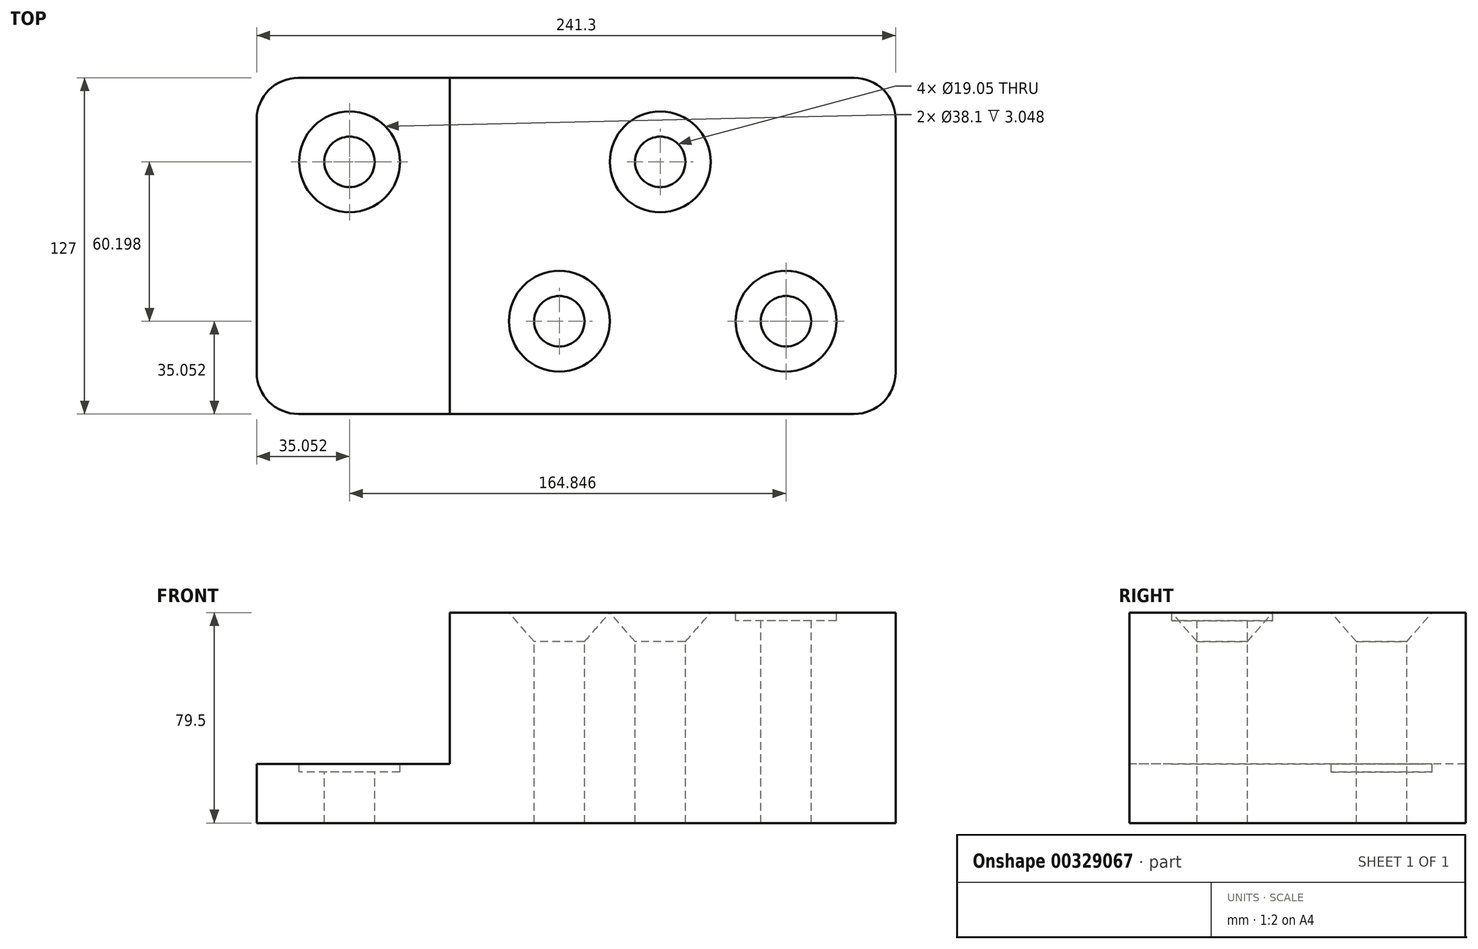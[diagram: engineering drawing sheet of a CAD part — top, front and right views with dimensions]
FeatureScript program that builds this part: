
annotation { "Feature Type Name" : "Feature", "Feature Type Description" : "" }
export const myFeature = defineFeature(function(context is Context, id is Id, definition is map)
    precondition{}
    {
        {
            var Q0;
            Q0=qCreatedBy(makeId("Top.planeOp"),FACE);
            var sketch = newSketch(context, id + "F0", { "sketchPlane" : qUnion([Q0])});
            skLineSegment(sketch, "E0.bottom", {"start": v(0, 0) * mm, "end": v(241.3, 0) * mm});
            skLineSegment(sketch, "E0.top", {"start": v(0, 127) * mm, "end": v(241.3, 127) * mm});
            skLineSegment(sketch, "E0.left", {"start": v(0, 0) * mm, "end": v(0, 127) * mm});
            skLineSegment(sketch, "E0.right", {"start": v(241.3, 0) * mm, "end": v(241.3, 127) * mm});
            skSolve(sketch);
        }
        {
            var Q0;
            Q0 = qSketchRegion(id + "F0", true);
            extrude(context, id + "F1", {"entities" : qUnion([Q0]), "depth" : 79.5 * mm});
        }
        {
            var Q0;
            Q0=makeQuery(id+"F1.opExtrude","CAP_FACE",FACE,{"disambiguationData":[OSD([sQuery(id+"F0.wireOp",EDGE,"E0.bottom"),sQuery(id+"F0.wireOp",EDGE,"E0.top"),sQuery(id+"F0.wireOp",EDGE,"E0.left"),sQuery(id+"F0.wireOp",EDGE,"E0.right")])],"isStart":false});
            var sketch = newSketch(context, id + "F2", { "sketchPlane" : qUnion([Q0])});
            skLineSegment(sketch, "E1.bottom", {"start": v(241.3, 127) * mm, "end": v(72.9, 127) * mm});
            skLineSegment(sketch, "E1.top", {"start": v(241.3, 0) * mm, "end": v(72.9, 0) * mm});
            skLineSegment(sketch, "E1.left", {"start": v(241.3, 127) * mm, "end": v(241.3, 0) * mm});
            skLineSegment(sketch, "E1.right", {"start": v(72.9, 127) * mm, "end": v(72.9, 0) * mm});
            skSolve(sketch);
        }
        {
            var Q0;
            {var subQ0=sQuery(id+"F2.wireOp",EDGE,"E1.right");Q0=makeQuery(id+"F2.imprint","IMPRINT",FACE,{"disambiguationData":[TD([[makeQuery(id+"F2.imprint","IMPRINT",EDGE,{"derivedFrom":subQ0}),-1.0]])]});}
            extrude(context, id + "F3", {"entities" : qUnion([Q0]), "operationType" : NewBodyOperationType.REMOVE, "oppositeDirection" : true, "depth" : 57.15 * mm});
        }
        {
            var Q0;
            Q0=makeQuery(id+"F3.boolean.opBoolean","COPY",EDGE,{"derivedFrom":makeQuery(id+"F3.opExtrude","SWEPT_EDGE",EDGE,{"disambiguationData":[OSD([sQuery(id+"F0.wireOp",EDGE,"E0.bottom"),sQuery(id+"F2.wireOp",EDGE,"E1.top"),sQuery(id+"F2.wireOp",EDGE,"E1.right")])]})});
            var Q1;
            Q1=makeQuery(id+"F1.opExtrude","SWEPT_EDGE",EDGE,{"disambiguationData":[OSD([sQuery(id+"F0.wireOp",EDGE,"E0.bottom"),sQuery(id+"F0.wireOp",EDGE,"E0.left")])]});
            var Q2;
            Q2=makeQuery(id+"F1.opExtrude","SWEPT_EDGE",EDGE,{"disambiguationData":[OSD([sQuery(id+"F0.wireOp",EDGE,"E0.top"),sQuery(id+"F0.wireOp",EDGE,"E0.left")])]});
            var Q3;
            Q3=makeQuery(id+"F3.boolean.opBoolean","COPY",EDGE,{"derivedFrom":makeQuery(id+"F3.opExtrude","SWEPT_EDGE",EDGE,{"disambiguationData":[OSD([sQuery(id+"F0.wireOp",EDGE,"E0.top"),sQuery(id+"F2.wireOp",EDGE,"E1.bottom"),sQuery(id+"F2.wireOp",EDGE,"E1.right")])]})});
            var Q4;
            Q4=makeQuery(id+"F1.opExtrude","SWEPT_EDGE",EDGE,{"disambiguationData":[OSD([sQuery(id+"F0.wireOp",EDGE,"E0.bottom"),sQuery(id+"F0.wireOp",EDGE,"E0.right")])]});
            var Q5;
            Q5=makeQuery(id+"F1.opExtrude","SWEPT_EDGE",EDGE,{"disambiguationData":[OSD([sQuery(id+"F0.wireOp",EDGE,"E0.top"),sQuery(id+"F0.wireOp",EDGE,"E0.right")])]});
            fillet(context, id + "F4", {"entities" : qUnion([Q0, Q1, Q2, Q3, Q4, Q5]), "radius" : 15.75 * mm, "tangentPropagation" : true, "allowEdgeOverflow" : false});
        }
        {
            var Q0;
            Q0=makeQuery(id+"F1.opExtrude","CAP_FACE",FACE,{"disambiguationData":[OSD([sQuery(id+"F0.wireOp",EDGE,"E0.bottom"),sQuery(id+"F0.wireOp",EDGE,"E0.top"),sQuery(id+"F0.wireOp",EDGE,"E0.left"),sQuery(id+"F0.wireOp",EDGE,"E0.right")])],"isStart":false});
            var sketch = newSketch(context, id + "F5", { "sketchPlane" : qUnion([Q0])});
            skPoint(sketch, "E2", {"position": v(199.9, 35.05) * mm});
            skPoint(sketch, "E3", {"position": v(152.4, 95.25) * mm});
            skPoint(sketch, "E4", {"position": v(114.3, 35.05) * mm});
            skSolve(sketch);
        }
        {
            var Q0;
            Q0=sQuery(id+"F5.wireOp",VERTEX,"E2");
            var Q1;
            Q1=makeQuery(id+"F1.opExtrude","SWEPT_BODY",BODY,{"disambiguationData":[OSD([sQuery(id+"F0.wireOp",EDGE,"E0.bottom"),sQuery(id+"F0.wireOp",EDGE,"E0.top"),sQuery(id+"F0.wireOp",EDGE,"E0.left"),sQuery(id+"F0.wireOp",EDGE,"E0.right")])]});
            hole(context, id + "F6", {"style" : HoleStyle.C_BORE, "endStyle" : HoleEndStyle.THROUGH, "holeDiameter" : 19.05 * mm, "cBoreDiameter" : 38.1 * mm, "cBoreDepth" : 3.05 * mm, "tappedDepth" : 12.7 * mm, "tapClearance" : 3, "locations" : qUnion([Q0]), "scope" : qUnion([Q1])});
        }
        {
            var Q0;
            Q0=makeQuery(id+"F1.opExtrude","CAP_FACE",FACE,{"disambiguationData":[OSD([sQuery(id+"F0.wireOp",EDGE,"E0.bottom"),sQuery(id+"F0.wireOp",EDGE,"E0.top"),sQuery(id+"F0.wireOp",EDGE,"E0.left"),sQuery(id+"F0.wireOp",EDGE,"E0.right")])],"isStart":false});
            var sketch = newSketch(context, id + "F7", { "sketchPlane" : qUnion([Q0])});
            skPoint(sketch, "E5", {"position": v(152.4, 95.25) * mm});
            skPoint(sketch, "E6", {"position": v(114.3, 35.05) * mm});
            skSolve(sketch);
        }
        {
            var Q0;
            Q0=sQuery(id+"F7.wireOp",VERTEX,"E5");
            var Q1;
            Q1=sQuery(id+"F7.wireOp",VERTEX,"E6");
            var Q2;
            Q2=makeQuery(id+"F1.opExtrude","SWEPT_BODY",BODY,{"disambiguationData":[OSD([sQuery(id+"F0.wireOp",EDGE,"E0.bottom"),sQuery(id+"F0.wireOp",EDGE,"E0.top"),sQuery(id+"F0.wireOp",EDGE,"E0.left"),sQuery(id+"F0.wireOp",EDGE,"E0.right")])]});
            hole(context, id + "F8", {"style" : HoleStyle.C_SINK, "endStyle" : HoleEndStyle.THROUGH, "holeDiameter" : 19.05 * mm, "cSinkDiameter" : 38.1 * mm, "cSinkAngle" : 82 * degree, "tappedDepth" : 12.7 * mm, "tapClearance" : 3, "locations" : qUnion([Q0, Q1]), "scope" : qUnion([Q2])});
        }
        {
            var Q0;
            Q0=makeQuery(id+"F3.boolean.opBoolean","COPY",FACE,{"derivedFrom":makeQuery(id+"F3.opExtrude","CAP_FACE",FACE,{"disambiguationData":[OSD([sQuery(id+"F0.wireOp",EDGE,"E0.bottom"),sQuery(id+"F0.wireOp",EDGE,"E0.top"),sQuery(id+"F0.wireOp",EDGE,"E0.left"),sQuery(id+"F2.wireOp",EDGE,"E1.right")])],"isStart":false})});
            var sketch = newSketch(context, id + "F9", { "sketchPlane" : qUnion([Q0])});
            skPoint(sketch, "E7", {"position": v(35.05, 95.25) * mm});
            skSolve(sketch);
        }
        {
            var Q0;
            Q0=sQuery(id+"F9.wireOp",VERTEX,"E7");
            var Q1;
            Q1=makeQuery(id+"F1.opExtrude","SWEPT_BODY",BODY,{"disambiguationData":[OSD([sQuery(id+"F0.wireOp",EDGE,"E0.bottom"),sQuery(id+"F0.wireOp",EDGE,"E0.top"),sQuery(id+"F0.wireOp",EDGE,"E0.left"),sQuery(id+"F0.wireOp",EDGE,"E0.right")])]});
            hole(context, id + "F10", {"style" : HoleStyle.C_BORE, "endStyle" : HoleEndStyle.THROUGH, "holeDiameter" : 19.05 * mm, "cBoreDiameter" : 38.1 * mm, "cBoreDepth" : 3.05 * mm, "tappedDepth" : 12.7 * mm, "tapClearance" : 3, "locations" : qUnion([Q0]), "scope" : qUnion([Q1])});
        }
    });
